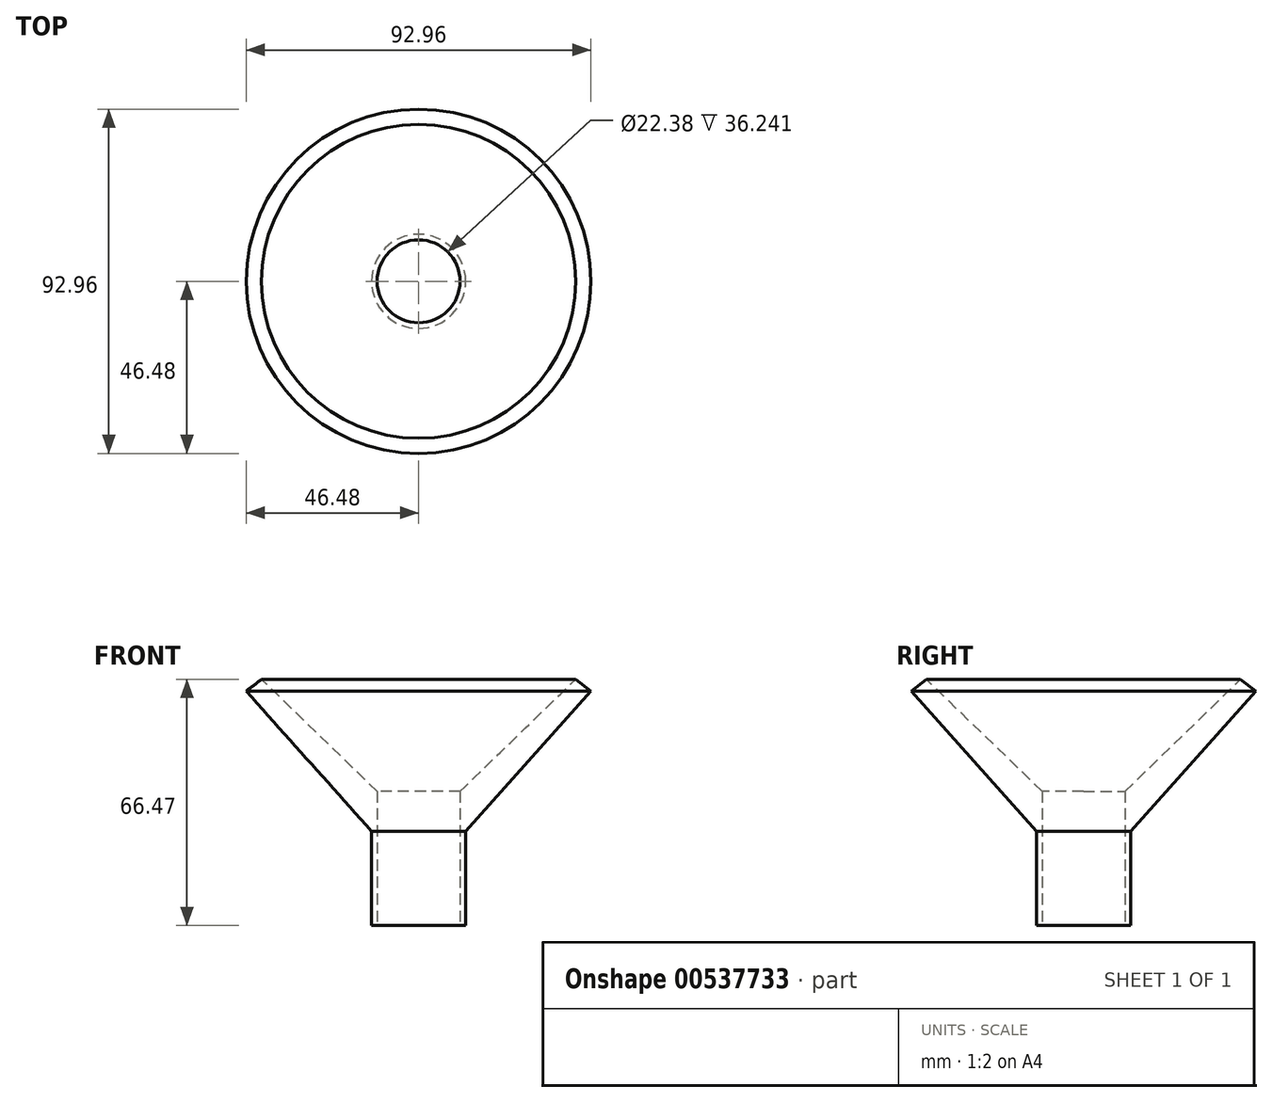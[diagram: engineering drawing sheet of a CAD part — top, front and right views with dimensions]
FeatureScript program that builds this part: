
annotation { "Feature Type Name" : "Feature", "Feature Type Description" : "" }
export const myFeature = defineFeature(function(context is Context, id is Id, definition is map)
    precondition{}
    {
        {
            var Q0;
            Q0=qCreatedBy(makeId("Front.planeOp"),FACE);
            var sketch = newSketch(context, id + "F0", { "sketchPlane" : qUnion([Q0])});
            skLineSegment(sketch, "E0", {"start": v(33.78, 37.94) * mm, "end": v(0, 0) * mm});
            skLineSegment(sketch, "E1", {"start": v(0, 0) * mm, "end": v(0, -25.4) * mm});
            skLineSegment(sketch, "E2", {"start": v(0, -25.4) * mm, "end": v(-12.7, -25.4) * mm});
            skLineSegment(sketch, "E3", {"start": v(-12.7, -25.4) * mm, "end": v(-12.7, 0) * mm});
            skLineSegment(sketch, "E4", {"start": v(-12.7, 0) * mm, "end": v(29.68, 41.07) * mm});
            skLineSegment(sketch, "E5", {"start": v(29.68, 41.07) * mm, "end": v(33.78, 37.94) * mm});
            skSolve(sketch);
        }
        {
            var Q0;
            Q0=makeQuery(id+"F0.imprint","IMPRINT",FACE,{"disambiguationData":[TD([[makeQuery(id+"F0.imprint","IMPRINT",EDGE,{"derivedFrom":sQuery(id+"F0.wireOp",EDGE,"E0")}),-1.0]])]});
            var Q1;
            Q1=sQuery(id+"F0.wireOp",EDGE,"E3");
            revolve(context, id + "F1", {"entities" : qUnion([Q0]), "axis" : qUnion([Q1]), "revolveType" : RevolveType.FULL});
        }
        {
            var Q0;
            Q0=makeQuery(id+"F1.opRevolve","SWEPT_FACE",FACE,{"disambiguationData":[OSD([sQuery(id+"F0.wireOp",EDGE,"E2")])]});
            var sketch = newSketch(context, id + "F2", { "sketchPlane" : qUnion([Q0])});
            skCircle(sketch, "E6", {"center": v(-12.7, 0) * mm, "radius": 11.19 * mm});
            skSolve(sketch);
        }
        {
            var Q0;
            Q0=makeQuery(id+"F2.imprint","IMPRINT",FACE,{"disambiguationData":[TD([[makeQuery(id+"F2.imprint","IMPRINT",EDGE,{"derivedFrom":sQuery(id+"F2.wireOp",EDGE,"E6")}),1.0]])]});
            extrude(context, id + "F3", {"entities" : qUnion([Q0]), "operationType" : NewBodyOperationType.REMOVE, "oppositeDirection" : true, "depth" : 76.2 * mm, "offsetDistance" : 25.4 * mm});
        }
    });
